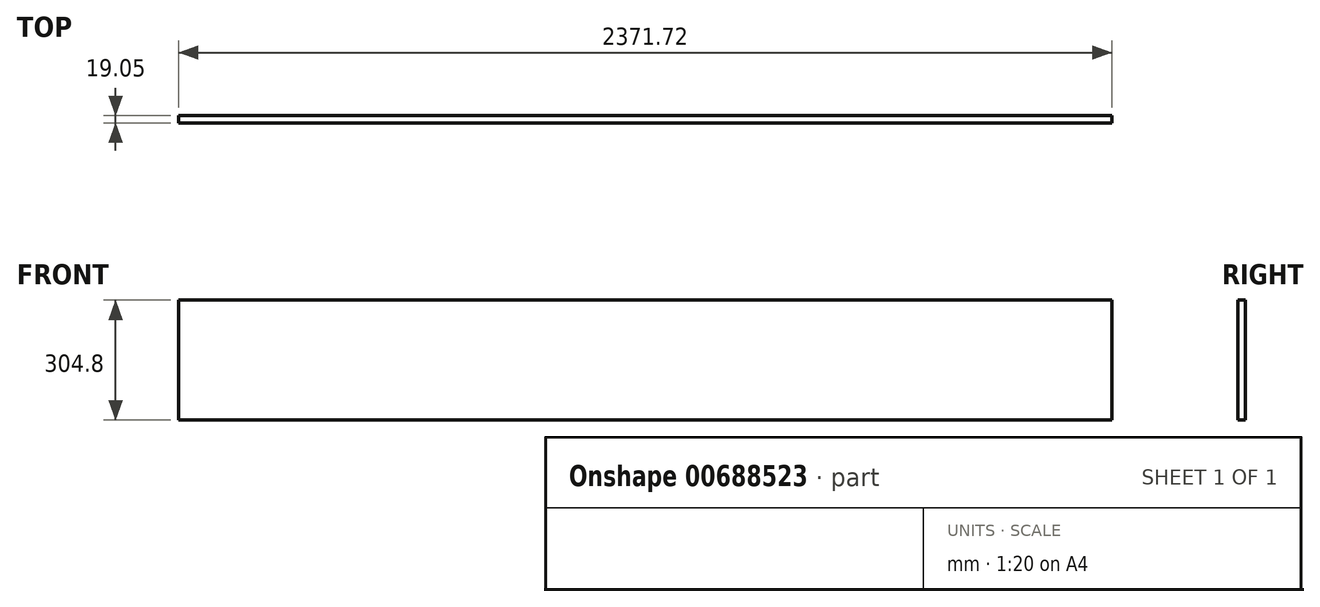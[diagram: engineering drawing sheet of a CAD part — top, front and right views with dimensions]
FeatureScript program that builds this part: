
annotation { "Feature Type Name" : "Feature", "Feature Type Description" : "" }
export const myFeature = defineFeature(function(context is Context, id is Id, definition is map)
    precondition{}
    {
        {
            var Q0;
            Q0=qCreatedBy(makeId("Front.planeOp"),FACE);
            var sketch = newSketch(context, id + "F0", { "sketchPlane" : qUnion([Q0])});
            skLineSegment(sketch, "E0.bottom", {"start": v(1185.86, 152.4) * mm, "end": v(-1185.86, 152.4) * mm});
            skLineSegment(sketch, "E0.top", {"start": v(1185.86, -152.4) * mm, "end": v(-1185.86, -152.4) * mm});
            skLineSegment(sketch, "E0.left", {"start": v(1185.86, 152.4) * mm, "end": v(1185.86, -152.4) * mm});
            skLineSegment(sketch, "E0.right", {"start": v(-1185.86, 152.4) * mm, "end": v(-1185.86, -152.4) * mm});
            skPoint(sketch, "E0.middle", {"position": v(0, 0) * mm});
            skSolve(sketch);
        }
        {
            var Q0;
            Q0=makeQuery(id+"F0.imprint","IMPRINT",FACE,{"disambiguationData":[TD([[makeQuery(id+"F0.imprint","IMPRINT",EDGE,{"derivedFrom":sQuery(id+"F0.wireOp",EDGE,"E0.bottom")}),1.0]])]});
            extrude(context, id + "F1", {"entities" : qUnion([Q0]), "depth" : 19.05 * mm, "offsetDistance" : 25.4 * mm});
        }
    });
